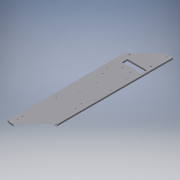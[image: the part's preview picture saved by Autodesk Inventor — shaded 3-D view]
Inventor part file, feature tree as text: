
AUTODESK INVENTOR PART (.ipt)
format: ipt  version: 2016 (Build 200138000, 138)  size: 371,712 bytes
history: native  units: in
note: dims shown in document units (in); Inventor stores cm internally (conversion verified against a paired STEP export)
features: extrude x21, sketch x21
ambient origin geometry x8: Origin, YZ Plane, XZ Plane, XY Plane, X Axis, Y Axis, Z Axis, Center Point
bodies: Solid1 (feature_tree)
feature tree (42):
  extrude  "Extrusion1"  Depth=3.94in
  extrude  "Extrusion3"  Depth=0.213in
  extrude  "Extrusion4"  Depth=2.9in
  extrude  "Extrusion5"  Depth=1.0in TaperAngle=0.0deg
  extrude  "Extrusion6"  Depth=0.25in
  extrude  "Extrusion7"  Depth=0.25in TaperAngle=0.0deg
  extrude  "Extrusion8"  Depth=0.1181in
  extrude  "Extrusion9"  Depth=2.147in TaperAngle=0.0deg
  extrude  "Extrusion10"  Depth=3.0in
  extrude  "Extrusion11"  Depth=0.477in
  extrude  "Extrusion12"  Depth=0.935in
  extrude  "Extrusion13"  Depth=0.3in
  extrude  "Extrusion14"  Depth=1.0in
  sketch  "Sketch17"  dims[d36=2.7in d37=0.7in]
  sketch  "Sketch18"  dims[d38=0.7in d39=2.7in]
  extrude  "Extrusion15"  Depth=0.7in
  extrude  "Extrusion16"  Depth=2.7in
  extrude  "Extrusion17"  Depth=0.1181in
  extrude  "Extrusion18"  Depth=0.1181in
  extrude  "Extrusion19"  Depth=0.15in
  extrude  "Extrusion20"  Depth=0.3in
  extrude  "Extrusion21"  Depth=0.3in
  extrude  "Extrusion22"  Depth=0.213in
  sketch  "Sketch1"  dims[d0=3.94in d1=14.0in]
  sketch  "Sketch5"  dims[d2=0.213in d3=0.0in d8=0.1181in]
  sketch  "Sketch6"  dims[d9=0.1181in d10=2.9in]
  sketch  "Sketch7"  dims[d11=0.379in d12=1.0in d13=0.0in]
  sketch  "Sketch8"  dims[d14=0.11in d15=0.25in]
  sketch  "Sketch9"  dims[d16=0.25in d17=1.0in d18=0.0in]
  sketch  "Sketch10"  dims[d19=0.1181in d20=0.1181in]
  sketch  "Sketch11"  dims[d21=10.0in d22=0.0in d23=2.147in d24=0.0in]
  sketch  "Sketch12"  dims[d25=2.147in d26=0.0in d27=3.0in]
  sketch  "Sketch13"  dims[d28=1.0in d29=0.477in]
  sketch  "Sketch14"  dims[d30=0.463in d31=0.935in]
  sketch  "Sketch15"  dims[d32=0.3in d33=0.3in]
  sketch  "Sketch16"  dims[d34=1.0in d35=1.0in]
  sketch  "Sketch19"  dims[d40=0.1181in d41=0.1181in]
  sketch  "Sketch20"  dims[d42=0.1181in d43=0.1181in]
  sketch  "Sketch21"  dims[d44=0.15in d45=1.0in]
  sketch  "Sketch22"  dims[d46=1.0in d47=0.3in]
  sketch  "Sketch23"  dims[d48=0.3in d49=0.3in]
  sketch  "Sketch24"  dims[d50=0.3in d51=3.0in d52=1.0in d53=1.0in d54=0.7in d55=2.147in d56=0.0in d57=5.579in d58=0.323in d59=0.086in d60=0.086in d62=2.036in d63=2.281in d64=2.281in d65=2.147in d66=0.0in d67=0.121in d68=0.341in d69=8.925in d75=1.0in d76=0.0in d89=0.599in d90=0.104in d91=2.958in d92=2.103in d93=0.08in d94=0.116in d95=1.472in d96=0.55in d97=2.958in d98=0.121in d99=0.104in d100=0.121in d101=0.104in d102=1.098in d103=0.297in d104=2.3788in d105=1.0in d106=0.0in d107=3.3244in d108=0.429in d109=0.5in d110=0.084in d111=0.084in d114=0.274in d115=1.0in d116=0.0in d117=0.1181in d119=4.148in d120=0.85in d121=0.1181in d122=0.941in d123=9.225in d124=1.0in d125=0.0in d128=7.3543in d129=2.887in d130=0.1181in d131=0.1181in d132=0.1181in d133=0.1181in d134=0.1181in d135=0.1181in d136=0.1181in d137=0.1181in d138=0.1181in d139=0.1181in d140=0.1181in d141=0.1181in d142=1.0in d143=0.0in d144=3.0in d145=0.0in d146=3.0in d147=0.0in d148=0.1181in d149=0.1181in d150=0.1181in d151=0.1181in d152=0.7in d153=0.7in d154=2.7in d155=2.7in d156=2.7in d157=1.0in d158=0.0in d159=0.213in d160=0.0in d161=0.1181in d162=0.1181in d163=1.098in d164=1.098in d165=0.213in d166=0.0in d167=0.213in d168=0.0in d169=0.15in d170=0.15in d171=0.213in d172=0.0in d173=0.899in d174=0.899in d175=0.213in d176=0.0in]
